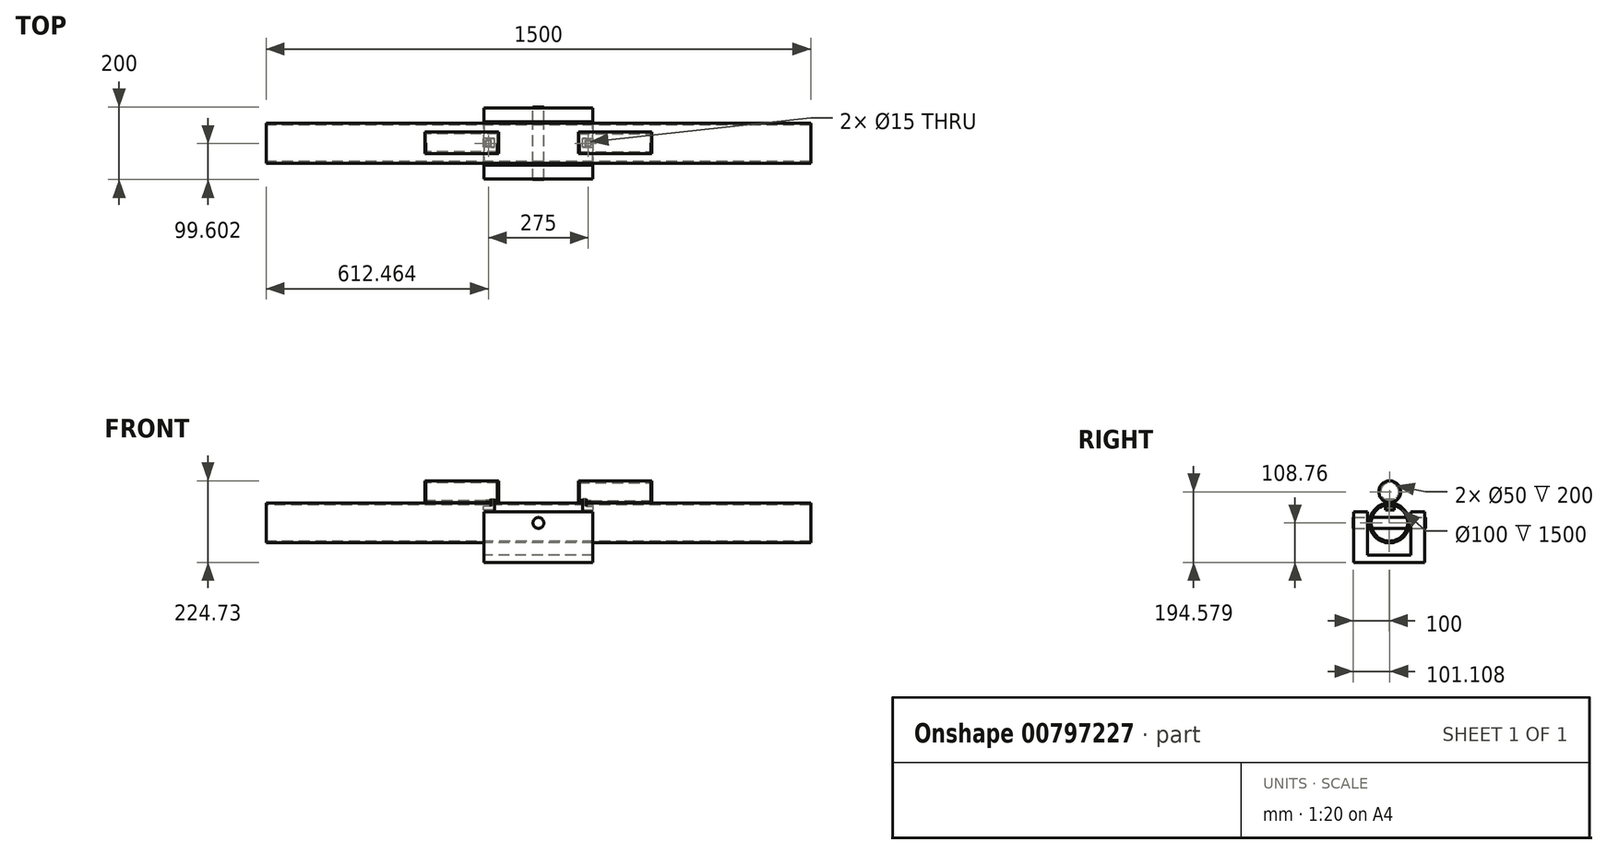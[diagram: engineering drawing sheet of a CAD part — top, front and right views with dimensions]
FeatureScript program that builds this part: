
annotation { "Feature Type Name" : "Feature", "Feature Type Description" : "" }
export const myFeature = defineFeature(function(context is Context, id is Id, definition is map)
    precondition{}
    {
        {
            var Q0;
            Q0=qCreatedBy(makeId("Right.planeOp"),FACE);
            var sketch = newSketch(context, id + "F0", { "sketchPlane" : qUnion([Q0])});
            skCircle(sketch, "E0", {"center": v(0, 0) * mm, "radius": 50 * mm});
            skCircle(sketch, "E1.0", {"center": v(0, 0) * mm, "radius": 55 * mm});
            skSolve(sketch);
        }
        {
            var Q0;
            Q0=makeQuery(id+"F0.imprint","IMPRINT",FACE,{"disambiguationData":[TD([[makeQuery(id+"F0.imprint","IMPRINT",EDGE,{"derivedFrom":sQuery(id+"F0.wireOp",EDGE,"E0")}),-1.0]])]});
            extrude(context, id + "F1", {"entities" : qUnion([Q0]), "depth" : 1500 * mm, "offsetDistance" : 25 * mm});
        }
        {
            var Q0;
            Q0=makeQuery(id+"F1.opExtrude","SWEPT_BODY",BODY,{"disambiguationData":[OSD([sQuery(id+"F0.wireOp",EDGE,"E0"),sQuery(id+"F0.wireOp",EDGE,"E1.0")])]});
            transform(context, id + "F2", {"entities" : qUnion([Q0]), "transformType" : TransformType.TRANSLATION_3D, "dx" : -750 * mm, "dy" : 0 * mm, "dz" : 0 * mm, "makeCopy" : false});
        }
        {
            var Q0;
            Q0=qCreatedBy(makeId("Right.planeOp"),FACE);
            var sketch = newSketch(context, id + "F3", { "sketchPlane" : qUnion([Q0])});
            skLineSegment(sketch, "E2", {"start": v(279.53, -27.76) * mm, "end": v(279.53, -147.76) * mm});
            skLineSegment(sketch, "E3", {"start": v(279.53, -147.76) * mm, "end": v(159.53, -147.76) * mm});
            skLineSegment(sketch, "E4", {"start": v(159.53, -147.76) * mm, "end": v(159.53, -27.76) * mm});
            skLineSegment(sketch, "E5", {"start": v(159.53, -27.76) * mm, "end": v(121.88, -27.76) * mm});
            skLineSegment(sketch, "E6", {"start": v(121.88, -27.76) * mm, "end": v(121.88, -167.76) * mm});
            skLineSegment(sketch, "E7", {"start": v(121.88, -167.76) * mm, "end": v(317.17, -167.76) * mm});
            skLineSegment(sketch, "E8", {"start": v(317.17, -167.76) * mm, "end": v(317.17, -27.76) * mm});
            skLineSegment(sketch, "E9", {"start": v(317.17, -27.76) * mm, "end": v(279.53, -27.76) * mm});
            skSolve(sketch);
        }
        {
            var Q0;
            Q0=makeQuery(id+"F3.imprint","IMPRINT",FACE,{"disambiguationData":[TD([[makeQuery(id+"F3.imprint","IMPRINT",EDGE,{"derivedFrom":sQuery(id+"F3.wireOp",EDGE,"E2")}),1.0]])]});
            extrude(context, id + "F4", {"entities" : qUnion([Q0]), "depth" : 300 * mm, "offsetDistance" : 25 * mm});
        }
        {
            var Q0;
            Q0=makeQuery(id+"F4.opExtrude","SWEPT_BODY",BODY,{"disambiguationData":[OSD([sQuery(id+"F3.wireOp",EDGE,"E2"),sQuery(id+"F3.wireOp",EDGE,"E3"),sQuery(id+"F3.wireOp",EDGE,"E4"),sQuery(id+"F3.wireOp",EDGE,"E5"),sQuery(id+"F3.wireOp",EDGE,"E6"),sQuery(id+"F3.wireOp",EDGE,"E7"),sQuery(id+"F3.wireOp",EDGE,"E8"),sQuery(id+"F3.wireOp",EDGE,"E9")])]});
            transform(context, id + "F5", {"entities" : qUnion([Q0]), "transformType" : TransformType.TRANSLATION_3D, "dx" : -150 * mm, "dy" : -220 * mm, "dz" : 59 * mm, "makeCopy" : false});
        }
        {
            var Q0;
            Q0=qCreatedBy(makeId("Front.planeOp"),FACE);
            var sketch = newSketch(context, id + "F6", { "sketchPlane" : qUnion([Q0])});
            skCircle(sketch, "E10", {"center": v(0, 0) * mm, "radius": 15 * mm});
            skSolve(sketch);
        }
        {
            var Q0;
            Q0 = qSketchRegion(id + "F6", true);
            var Q1;
            Q1 = qSketchRegion(id + "F8", true);
            extrude(context, id + "F7", {"entities" : qUnion([Q0, Q1]), "depth" : 100 * mm, "offsetDistance" : 25 * mm, "hasSecondDirection" : true, "secondDirectionOppositeDirection" : true, "secondDirectionDepth" : 100 * mm});
        }
        {
            var Q0;
            Q0=qCreatedBy(makeId("Right.planeOp"),FACE);
            var sketch = newSketch(context, id + "F8", { "sketchPlane" : qUnion([Q0])});
            skCircle(sketch, "E11", {"center": v(8.1, 102.82) * mm, "radius": 30 * mm});
            skCircle(sketch, "E12.0", {"center": v(8.1, 102.82) * mm, "radius": 25 * mm});
            skSolve(sketch);
        }
        {
            var Q0;
            Q0=makeQuery(id+"F8.imprint","IMPRINT",FACE,{"disambiguationData":[TD([[makeQuery(id+"F8.imprint","IMPRINT",EDGE,{"derivedFrom":sQuery(id+"F8.wireOp",EDGE,"E11")}),1.0]])]});
            extrude(context, id + "F9", {"entities" : qUnion([Q0]), "depth" : 200 * mm, "offsetDistance" : 25 * mm});
        }
        {
            var Q0;
            Q0=makeQuery(id+"F9.opExtrude","SWEPT_BODY",BODY,{"disambiguationData":[OSD([sQuery(id+"F8.wireOp",EDGE,"E11")])]});
            transform(context, id + "F10", {"entities" : qUnion([Q0]), "transformType" : TransformType.TRANSLATION_3D, "dx" : -421 * mm, "dy" : -7 * mm, "dz" : 60 * mm, "makeCopy" : false});
        }
        {
            var Q0;
            Q0=qCreatedBy(makeId("Front.planeOp"),FACE);
            var sketch = newSketch(context, id + "F11", { "sketchPlane" : qUnion([Q0])});
            skLineSegment(sketch, "E13", {"start": v(-19.33, 103.08) * mm, "end": v(-19.33, 83.08) * mm});
            skLineSegment(sketch, "E14", {"start": v(-19.33, 83.08) * mm, "end": v(-39.33, 83.08) * mm});
            skLineSegment(sketch, "E15", {"start": v(-19.33, 103.08) * mm, "end": v(-9.33, 103.08) * mm});
            skLineSegment(sketch, "E16", {"start": v(-9.33, 103.08) * mm, "end": v(-9.33, 73.08) * mm});
            skLineSegment(sketch, "E17", {"start": v(-9.33, 73.08) * mm, "end": v(-39.33, 73.08) * mm});
            skLineSegment(sketch, "E18", {"start": v(-39.33, 73.08) * mm, "end": v(-39.33, 83.08) * mm});
            skSolve(sketch);
        }
        {
            var Q0;
            Q0=makeQuery(id+"F9.opExtrude","CAP_FACE",FACE,{"disambiguationData":[OSD([sQuery(id+"F8.wireOp",EDGE,"E11"),sQuery(id+"F8.wireOp",EDGE,"E12.0")])],"isStart":true});
            cPlane(context, id + "F12", {"entities" : qUnion([Q0]), "cplaneType" : CPlaneType.OFFSET, "offset" : 25 * mm, "width" : 150 * mm, "height" : 150 * mm});
        }
        {
            var Q0;
            Q0=qCreatedBy(id+"F12.planeOp",FACE);
            var sketch = newSketch(context, id + "F13", { "sketchPlane" : qUnion([Q0])});
            skCircle(sketch, "E19", {"center": v(0, 176.37) * mm, "radius": 30 * mm});
            skSolve(sketch);
        }
        {
            var Q0;
            Q0=makeQuery(id+"F13.imprint","IMPRINT",FACE,{"disambiguationData":[TD([[makeQuery(id+"F13.imprint","IMPRINT",EDGE,{"derivedFrom":sQuery(id+"F13.wireOp",EDGE,"E19")}),1.0]])]});
            extrude(context, id + "F14", {"entities" : qUnion([Q0]), "depth" : 3 * mm, "offsetDistance" : 25 * mm});
        }
        {
            var Q0;
            Q0=makeQuery(id+"F14.opExtrude","SWEPT_BODY",BODY,{"disambiguationData":[OSD([sQuery(id+"F13.wireOp",EDGE,"E19")])]});
            transform(context, id + "F15", {"entities" : qUnion([Q0]), "transformType" : TransformType.TRANSLATION_3D, "dx" : 26.1 * mm, "dy" : 0.9 * mm, "dz" : -13.4 * mm, "makeCopy" : false});
        }
        {
            var Q0;
            Q0=makeQuery(id+"F14.opExtrude","SWEPT_BODY",BODY,{"disambiguationData":[OSD([sQuery(id+"F13.wireOp",EDGE,"E19")])]});
            transform(context, id + "F16", {"entities" : qUnion([Q0]), "transformType" : TransformType.TRANSLATION_3D, "dx" : 200 * mm, "dy" : 0 * mm, "dz" : 0 * mm, "makeCopy" : true});
        }
        {
            var Q0;
            Q0=makeQuery(id+"F11.imprint","IMPRINT",FACE,{"disambiguationData":[TD([[makeQuery(id+"F11.imprint","IMPRINT",EDGE,{"derivedFrom":sQuery(id+"F11.wireOp",EDGE,"E13")}),1.0]])]});
            extrude(context, id + "F17", {"entities" : qUnion([Q0]), "depth" : 25 * mm, "offsetDistance" : 25 * mm});
        }
        {
            var Q0;
            Q0=makeQuery(id+"F17.opExtrude","SWEPT_BODY",BODY,{"disambiguationData":[OSD([sQuery(id+"F11.wireOp",EDGE,"E13"),sQuery(id+"F11.wireOp",EDGE,"E14"),sQuery(id+"F11.wireOp",EDGE,"E15"),sQuery(id+"F11.wireOp",EDGE,"E16"),sQuery(id+"F11.wireOp",EDGE,"E17"),sQuery(id+"F11.wireOp",EDGE,"E18")])]});
            transform(context, id + "F18", {"entities" : qUnion([Q0]), "transformType" : TransformType.TRANSLATION_3D, "dx" : 0 * mm, "dy" : 0 * mm, "dz" : 60 * mm, "makeCopy" : true});
        }
        {
            var Q0;
            Q0=makeQuery(id+"F18.opPattern","COPY",BODY,{"derivedFrom":makeQuery(id+"F17.opExtrude","SWEPT_BODY",BODY,{"disambiguationData":[OSD([sQuery(id+"F11.wireOp",EDGE,"E13"),sQuery(id+"F11.wireOp",EDGE,"E14"),sQuery(id+"F11.wireOp",EDGE,"E15"),sQuery(id+"F11.wireOp",EDGE,"E16"),sQuery(id+"F11.wireOp",EDGE,"E17"),sQuery(id+"F11.wireOp",EDGE,"E18")])]}),"instanceName":"1"});
            transform(context, id + "F19", {"entities" : qUnion([Q0]), "transformType" : TransformType.TRANSLATION_3D, "dx" : -225 * mm, "dy" : 14 * mm, "dz" : -21.2 * mm, "makeCopy" : false});
        }
        {
            var Q0;
            Q0=makeQuery(id+"F9.opExtrude","SWEPT_BODY",BODY,{"disambiguationData":[OSD([sQuery(id+"F8.wireOp",EDGE,"E11"),sQuery(id+"F8.wireOp",EDGE,"E12.0")])]});
            var Q1;
            Q1=makeQuery(id+"F16.opPattern","COPY",BODY,{"derivedFrom":makeQuery(id+"F14.opExtrude","SWEPT_BODY",BODY,{"disambiguationData":[OSD([sQuery(id+"F13.wireOp",EDGE,"E19")])]}),"instanceName":"1"});
            var Q2;
            Q2=makeQuery(id+"F18.opPattern","COPY",BODY,{"derivedFrom":makeQuery(id+"F17.opExtrude","SWEPT_BODY",BODY,{"disambiguationData":[OSD([sQuery(id+"F11.wireOp",EDGE,"E13"),sQuery(id+"F11.wireOp",EDGE,"E14"),sQuery(id+"F11.wireOp",EDGE,"E15"),sQuery(id+"F11.wireOp",EDGE,"E16"),sQuery(id+"F11.wireOp",EDGE,"E17"),sQuery(id+"F11.wireOp",EDGE,"E18")])]}),"instanceName":"1"});
            var Q3;
            Q3=makeQuery(id+"F14.opExtrude","SWEPT_BODY",BODY,{"disambiguationData":[OSD([sQuery(id+"F13.wireOp",EDGE,"E19")])]});
            transform(context, id + "F20", {"entities" : qUnion([Q0, Q1, Q2, Q3]), "transformType" : TransformType.TRANSLATION_3D, "dx" : 110 * mm, "dy" : 0 * mm, "dz" : 0 * mm, "makeCopy" : false});
        }
        {
            var Q0;
            Q0=makeQuery(id+"F17.opExtrude","SWEPT_BODY",BODY,{"disambiguationData":[OSD([sQuery(id+"F11.wireOp",EDGE,"E13"),sQuery(id+"F11.wireOp",EDGE,"E14"),sQuery(id+"F11.wireOp",EDGE,"E15"),sQuery(id+"F11.wireOp",EDGE,"E16"),sQuery(id+"F11.wireOp",EDGE,"E17"),sQuery(id+"F11.wireOp",EDGE,"E18")])]});
            deleteBodies(context, id + "F21", {"entities" : qUnion([Q0])});
        }
        {
            var Q0;
            Q0=makeQuery(id+"F18.opPattern","COPY",BODY,{"derivedFrom":makeQuery(id+"F17.opExtrude","SWEPT_BODY",BODY,{"disambiguationData":[OSD([sQuery(id+"F11.wireOp",EDGE,"E13"),sQuery(id+"F11.wireOp",EDGE,"E14"),sQuery(id+"F11.wireOp",EDGE,"E15"),sQuery(id+"F11.wireOp",EDGE,"E16"),sQuery(id+"F11.wireOp",EDGE,"E17"),sQuery(id+"F11.wireOp",EDGE,"E18")])]}),"instanceName":"1"});
            transform(context, id + "F22", {"entities" : qUnion([Q0]), "transformType" : TransformType.TRANSLATION_3D, "dx" : 232 * mm, "dy" : 0 * mm, "dz" : 67 * mm, "makeCopy" : false});
        }
        {
            var Q0;
            Q0=qCreatedBy(makeId("Top.planeOp"),FACE);
            var sketch = newSketch(context, id + "F23", { "sketchPlane" : qUnion([Q0])});
            skLineSegment(sketch, "E20.bottom", {"start": v(-233.93, 115.02) * mm, "end": v(-218.93, 115.02) * mm});
            skLineSegment(sketch, "E20.top", {"start": v(-233.93, 100.02) * mm, "end": v(-218.93, 100.02) * mm});
            skLineSegment(sketch, "E20.left", {"start": v(-233.93, 115.02) * mm, "end": v(-233.93, 100.02) * mm});
            skLineSegment(sketch, "E20.right", {"start": v(-218.93, 115.02) * mm, "end": v(-218.93, 100.02) * mm});
            skSolve(sketch);
        }
        {
            var Q0;
            Q0 = qSketchRegion(id + "F23", true);
            extrude(context, id + "F24", {"entities" : qUnion([Q0]), "depth" : 10 * mm, "offsetDistance" : 25 * mm});
        }
        {
            var Q0;
            Q0=makeQuery(id+"F24.opExtrude","SWEPT_BODY",BODY,{"disambiguationData":[OSD([sQuery(id+"F23.wireOp",EDGE,"E20.bottom"),sQuery(id+"F23.wireOp",EDGE,"E20.top"),sQuery(id+"F23.wireOp",EDGE,"E20.left"),sQuery(id+"F23.wireOp",EDGE,"E20.right")])]});
            transform(context, id + "F25", {"entities" : qUnion([Q0]), "transformType" : TransformType.TRANSLATION_3D, "dx" : 89 * mm, "dy" : -106.8 * mm, "dz" : 129 * mm, "makeCopy" : false});
        }
        {
            var Q0;
            Q0=makeQuery(id+"F24.opExtrude","SWEPT_BODY",BODY,{"disambiguationData":[OSD([sQuery(id+"F23.wireOp",EDGE,"E20.bottom"),sQuery(id+"F23.wireOp",EDGE,"E20.top"),sQuery(id+"F23.wireOp",EDGE,"E20.left"),sQuery(id+"F23.wireOp",EDGE,"E20.right")])]});
            var Q1;
            Q1=makeQuery(id+"F9.opExtrude","SWEPT_BODY",BODY,{"disambiguationData":[OSD([sQuery(id+"F8.wireOp",EDGE,"E11"),sQuery(id+"F8.wireOp",EDGE,"E12.0")])]});
            booleanBodies(context, id + "F26", {"operationType" : BooleanOperationType.SUBTRACTION, "tools" : qUnion([Q0]), "targets" : qUnion([Q1])});
        }
        {
            var Q0;
            Q0=makeQuery(id+"F18.opPattern","COPY",BODY,{"derivedFrom":makeQuery(id+"F17.opExtrude","SWEPT_BODY",BODY,{"disambiguationData":[OSD([sQuery(id+"F11.wireOp",EDGE,"E13"),sQuery(id+"F11.wireOp",EDGE,"E14"),sQuery(id+"F11.wireOp",EDGE,"E15"),sQuery(id+"F11.wireOp",EDGE,"E16"),sQuery(id+"F11.wireOp",EDGE,"E17"),sQuery(id+"F11.wireOp",EDGE,"E18")])]}),"instanceName":"1"});
            transform(context, id + "F27", {"entities" : qUnion([Q0]), "transformType" : TransformType.TRANSLATION_3D, "dx" : -229.1 * mm, "dy" : 0 * mm, "dz" : -66 * mm, "makeCopy" : false});
        }
        {
            var Q0;
            Q0=makeQuery(id+"F9.opExtrude","SWEPT_BODY",BODY,{"disambiguationData":[OSD([sQuery(id+"F8.wireOp",EDGE,"E11"),sQuery(id+"F8.wireOp",EDGE,"E12.0")])]});
            var Q1;
            Q1=makeQuery(id+"F16.opPattern","COPY",BODY,{"derivedFrom":makeQuery(id+"F14.opExtrude","SWEPT_BODY",BODY,{"disambiguationData":[OSD([sQuery(id+"F13.wireOp",EDGE,"E19")])]}),"instanceName":"1"});
            var Q2;
            Q2=makeQuery(id+"F18.opPattern","COPY",BODY,{"derivedFrom":makeQuery(id+"F17.opExtrude","SWEPT_BODY",BODY,{"disambiguationData":[OSD([sQuery(id+"F11.wireOp",EDGE,"E13"),sQuery(id+"F11.wireOp",EDGE,"E14"),sQuery(id+"F11.wireOp",EDGE,"E15"),sQuery(id+"F11.wireOp",EDGE,"E16"),sQuery(id+"F11.wireOp",EDGE,"E17"),sQuery(id+"F11.wireOp",EDGE,"E18")])]}),"instanceName":"1"});
            var Q3;
            Q3=makeQuery(id+"F14.opExtrude","SWEPT_BODY",BODY,{"disambiguationData":[OSD([sQuery(id+"F13.wireOp",EDGE,"E19")])]});
            var Q4;
            Q4=qCreatedBy(makeId("Right.planeOp"),FACE);
            mirror(context, id + "F28", {"entities" : qUnion([Q0, Q1, Q2, Q3]), "mirrorPlane" : qUnion([Q4])});
        }
        {
            var Q0;
            Q0=qCreatedBy(makeId("Top.planeOp"),FACE);
            var sketch = newSketch(context, id + "F29", { "sketchPlane" : qUnion([Q0])});
            skCircle(sketch, "E21", {"center": v(-268.54, 105.6) * mm, "radius": 7.5 * mm});
            skSolve(sketch);
        }
        {
            var Q0;
            Q0=makeQuery(id+"F29.imprint","IMPRINT",FACE,{"disambiguationData":[TD([[makeQuery(id+"F29.imprint","IMPRINT",EDGE,{"derivedFrom":sQuery(id+"F29.wireOp",EDGE,"E21")}),1.0]])]});
            extrude(context, id + "F30", {"entities" : qUnion([Q0]), "depth" : 10 * mm, "offsetDistance" : 25 * mm});
        }
        {
            var Q0;
            Q0=makeQuery(id+"F30.opExtrude","SWEPT_BODY",BODY,{"disambiguationData":[OSD([sQuery(id+"F29.wireOp",EDGE,"E21")])]});
            transform(context, id + "F31", {"entities" : qUnion([Q0]), "transformType" : TransformType.TRANSLATION_3D, "dx" : 131 * mm, "dy" : -106 * mm, "dz" : 48 * mm, "makeCopy" : false});
        }
        {
            var Q0;
            Q0=makeQuery(id+"F30.opExtrude","SWEPT_BODY",BODY,{"disambiguationData":[OSD([sQuery(id+"F29.wireOp",EDGE,"E21")])]});
            transform(context, id + "F32", {"entities" : qUnion([Q0]), "transformType" : TransformType.TRANSLATION_3D, "dx" : 275 * mm, "dy" : 0 * mm, "dz" : 0 * mm, "makeCopy" : true});
        }
        {
            var Q0;
            Q0=makeQuery(id+"F30.opExtrude","SWEPT_BODY",BODY,{"disambiguationData":[OSD([sQuery(id+"F29.wireOp",EDGE,"E21")])]});
            var Q1;
            Q1=makeQuery(id+"F32.opPattern","COPY",BODY,{"derivedFrom":makeQuery(id+"F30.opExtrude","SWEPT_BODY",BODY,{"disambiguationData":[OSD([sQuery(id+"F29.wireOp",EDGE,"E21")])]}),"instanceName":"1"});
            var Q2;
            Q2=makeQuery(id+"F1.opExtrude","SWEPT_BODY",BODY,{"disambiguationData":[OSD([sQuery(id+"F0.wireOp",EDGE,"E0"),sQuery(id+"F0.wireOp",EDGE,"E1.0")])]});
            booleanBodies(context, id + "F33", {"operationType" : BooleanOperationType.SUBTRACTION, "tools" : qUnion([Q0, Q1]), "targets" : qUnion([Q2])});
        }
        {
            var Q0;
            Q0=makeQuery(id+"F9.opExtrude","SWEPT_BODY",BODY,{"disambiguationData":[OSD([sQuery(id+"F8.wireOp",EDGE,"E11"),sQuery(id+"F8.wireOp",EDGE,"E12.0")])]});
            var Q1;
            Q1=makeQuery(id+"F16.opPattern","COPY",BODY,{"derivedFrom":makeQuery(id+"F14.opExtrude","SWEPT_BODY",BODY,{"disambiguationData":[OSD([sQuery(id+"F13.wireOp",EDGE,"E19")])]}),"instanceName":"1"});
            var Q2;
            Q2=makeQuery(id+"F28.opPattern","COPY",BODY,{"derivedFrom":makeQuery(id+"F9.opExtrude","SWEPT_BODY",BODY,{"disambiguationData":[OSD([sQuery(id+"F8.wireOp",EDGE,"E11"),sQuery(id+"F8.wireOp",EDGE,"E12.0")])]}),"instanceName":"1"});
            var Q3;
            Q3=makeQuery(id+"F18.opPattern","COPY",BODY,{"derivedFrom":makeQuery(id+"F17.opExtrude","SWEPT_BODY",BODY,{"disambiguationData":[OSD([sQuery(id+"F11.wireOp",EDGE,"E13"),sQuery(id+"F11.wireOp",EDGE,"E14"),sQuery(id+"F11.wireOp",EDGE,"E15"),sQuery(id+"F11.wireOp",EDGE,"E16"),sQuery(id+"F11.wireOp",EDGE,"E17"),sQuery(id+"F11.wireOp",EDGE,"E18")])]}),"instanceName":"1"});
            var Q4;
            Q4=makeQuery(id+"F14.opExtrude","SWEPT_BODY",BODY,{"disambiguationData":[OSD([sQuery(id+"F13.wireOp",EDGE,"E19")])]});
            var Q5;
            Q5=makeQuery(id+"F28.opPattern","COPY",BODY,{"derivedFrom":makeQuery(id+"F14.opExtrude","SWEPT_BODY",BODY,{"disambiguationData":[OSD([sQuery(id+"F13.wireOp",EDGE,"E19")])]}),"instanceName":"1"});
            var Q6;
            Q6=makeQuery(id+"F28.opPattern","COPY",BODY,{"derivedFrom":makeQuery(id+"F16.opPattern","COPY",BODY,{"derivedFrom":makeQuery(id+"F14.opExtrude","SWEPT_BODY",BODY,{"disambiguationData":[OSD([sQuery(id+"F13.wireOp",EDGE,"E19")])]}),"instanceName":"1"}),"instanceName":"1"});
            var Q7;
            Q7=makeQuery(id+"F28.opPattern","COPY",BODY,{"derivedFrom":makeQuery(id+"F18.opPattern","COPY",BODY,{"derivedFrom":makeQuery(id+"F17.opExtrude","SWEPT_BODY",BODY,{"disambiguationData":[OSD([sQuery(id+"F11.wireOp",EDGE,"E13"),sQuery(id+"F11.wireOp",EDGE,"E14"),sQuery(id+"F11.wireOp",EDGE,"E15"),sQuery(id+"F11.wireOp",EDGE,"E16"),sQuery(id+"F11.wireOp",EDGE,"E17"),sQuery(id+"F11.wireOp",EDGE,"E18")])]}),"instanceName":"1"}),"instanceName":"1"});
            transform(context, id + "F34", {"entities" : qUnion([Q0, Q1, Q2, Q3, Q4, Q5, Q6, Q7]), "transformType" : TransformType.TRANSLATION_3D, "dx" : 0 * mm, "dy" : 0 * mm, "dz" : -77 * mm, "makeCopy" : false});
        }
    });
